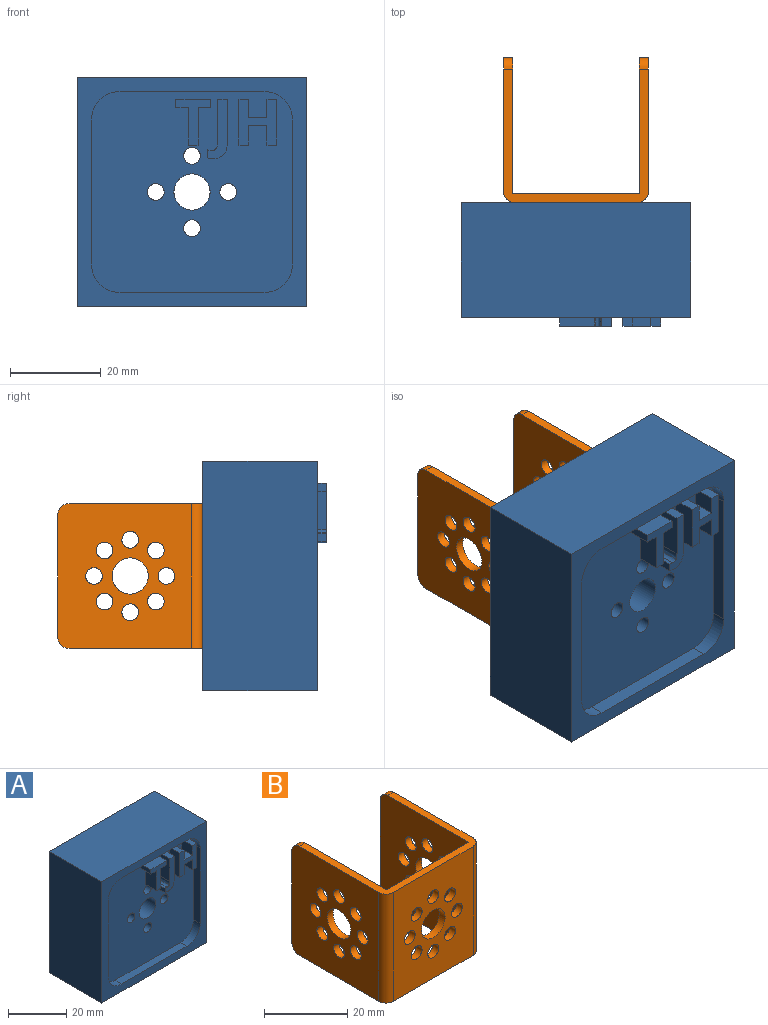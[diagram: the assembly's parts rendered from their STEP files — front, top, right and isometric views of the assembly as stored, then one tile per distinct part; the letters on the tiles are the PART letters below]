
ASSEMBLY  parts=2 mates=1
PART A: 53 faces, bbox 50.8x27.3x50.8 mm
  f0: plane 44.45x44.45mm, normal (0,-1,0), area 1734.2mm2, adj f7,f8,f9,f10,f11,f12,f13,f14
  f1: plane 50.8x50.8mm, normal (0,1,0), area 2487.4mm2, adj f2,f3,f4,f5,f15,f16,f17,f18
  f2: plane 50.8x25.4mm, normal (-1,0,0), area 1290.3mm2, adj f1,f3,f5,f6
  f3: plane 50.8x25.4mm, normal (0,0,-1), area 1290.3mm2, adj f1,f2,f4,f6
  f4: plane 50.8x25.4mm, normal (1,0,0), area 1290.3mm2, adj f1,f3,f5,f6
  f5: plane 50.8x25.4mm, normal (0,0,1), area 1290.3mm2, adj f1,f2,f4,f6
  f6: plane 50.8x50.8mm, normal (0,-1,0), area 639.5mm2, adj f2,f3,f4,f5,f7,f8,f9,f10
  f7: plane 31.75x3.18mm, normal (0,0,1), area 100.8mm2, adj f0,f6,f8,f14
  f8: cylinder r=6.35mm len=6.35mm, axis (0,-1,0), area 31.7mm2, adj f0,f6,f7,f9
  f9: plane 31.75x3.18mm, normal (-1,0,0), area 100.8mm2, adj f0,f6,f8,f10
  f10: cylinder r=6.35mm len=6.35mm, axis (0,-1,0), area 31.7mm2, adj f0,f6,f9,f11
  f11: plane 31.75x3.18mm, normal (0,0,-1), area 100.8mm2, adj f0,f6,f10,f12
  f12: cylinder r=6.35mm len=6.35mm, axis (0,-1,0), area 31.7mm2, adj f0,f6,f11,f13
  f13: plane 31.75x3.18mm, normal (1,0,0), area 100.8mm2, adj f0,f6,f12,f14
  f14: cylinder r=6.35mm len=6.35mm, axis (0,-1,0), area 31.7mm2, adj f0,f6,f7,f13
  f15: cylinder r=1.85mm len=22.23mm, axis (0,1,0), area 258.3mm2, adj f0,f1
  f16: cylinder r=4mm len=22.23mm, axis (0,1,0), area 558.6mm2, adj f0,f1
  f17: cylinder r=1.85mm len=22.23mm, axis (0,1,0), area 258.3mm2, adj f0,f1
  f18: cylinder r=1.85mm len=22.23mm, axis (0,1,0), area 258.3mm2, adj f0,f1
  f19: cylinder r=1.85mm len=22.23mm, axis (0,1,0), area 258.3mm2, adj f0,f1
  f20: plane 5.08x2.16mm, normal (0,0,-1), area 10.9mm2, adj f0,f21,f27,f28
  f21: plane 8.37x5.08mm, normal (1,0,0), area 42.5mm2, adj f0,f20,f22,f28
  f22: plane 5.08x2.76mm, normal (0,0,-1), area 14mm2, adj f0,f21,f23,f28
  f23: plane 5.08x1.79mm, normal (1,0,0), area 9.1mm2, adj f0,f22,f24,f28
  f24: plane 7.67x5.08mm, normal (0,0,1), area 39mm2, adj f0,f23,f25,f28
  f25: plane 5.08x1.79mm, normal (-1,0,0), area 9.1mm2, adj f0,f24,f26,f28
  f26: plane 5.08x2.76mm, normal (0,0,-1), area 14mm2, adj f0,f25,f27,f28
  f27: plane 8.37x5.08mm, normal (-1,0,0), area 42.5mm2, adj f0,f20,f26,f28
  f28: plane 10.16x7.67mm, normal (0,-1,0), area 31.8mm2, adj f20,f21,f22,f23,f24,f25,f26,f27
  f29: extruded ~5.08x1.27mm, area 6.5mm2, adj f0,f30,f38,f39
  f30: extruded ~5.08x2.41mm, area 13.5mm2, adj f0,f29,f31,f39
  f31: extruded ~5.08x2.71mm, area 14.7mm2, adj f0,f30,f32,f39
  f32: plane 9.51x5.08mm, normal (1,0,0), area 48.3mm2, adj f0,f31,f33,f39
  f33: plane 5.08x2.16mm, normal (0,0,1), area 10.9mm2, adj f0,f32,f34,f39
  f34: plane 9.52x5.08mm, normal (-1,0,0), area 48.4mm2, adj f0,f33,f35,f39
  f35: extruded ~5.08x1.38mm, area 7.3mm2, adj f0,f34,f36,f39
  f36: extruded ~5.08x1.02mm, area 5.9mm2, adj f0,f35,f37,f39
  f37: extruded ~5.08x1.01mm, area 5.2mm2, adj f0,f36,f38,f39
  f38: plane 5.08x1.79mm, normal (-1,0,0), area 9.1mm2, adj f0,f29,f37,f39
  f39: plane 13.15x4.49mm, normal (0,-1,0), area 30.9mm2, adj f29,f30,f31,f32,f33,f34,f35,f36
  f40: plane 5.08x2.15mm, normal (0,0,-1), area 10.9mm2, adj f0,f41,f51,f52
  f41: plane 10.16x5.08mm, normal (1,0,0), area 51.6mm2, adj f0,f40,f42,f52
  f42: plane 5.08x2.15mm, normal (0,0,1), area 10.9mm2, adj f0,f41,f43,f52
  f43: plane 5.08x3.98mm, normal (-1,0,0), area 20.2mm2, adj f0,f42,f44,f52
  f44: plane 5.08x4.02mm, normal (0,0,1), area 20.4mm2, adj f0,f43,f45,f52
  f45: plane 5.08x3.98mm, normal (1,0,0), area 20.2mm2, adj f0,f44,f46,f52
  f46: plane 5.08x2.16mm, normal (0,0,1), area 10.9mm2, adj f0,f45,f47,f52
  f47: plane 10.16x5.08mm, normal (-1,0,0), area 51.6mm2, adj f0,f46,f48,f52
  f48: plane 5.08x2.16mm, normal (0,0,-1), area 10.9mm2, adj f0,f47,f49,f52
  f49: plane 5.08x4.39mm, normal (1,0,0), area 22.3mm2, adj f0,f48,f50,f52
  f50: plane 5.08x4.02mm, normal (0,0,-1), area 20.4mm2, adj f0,f49,f51,f52
  f51: plane 5.08x4.39mm, normal (-1,0,0), area 22.3mm2, adj f0,f40,f50,f52
  f52: plane 10.16x8.33mm, normal (0,-1,0), area 51mm2, adj f40,f41,f42,f43,f44,f45,f46,f47
PART B: 43 faces, bbox 32x32x32 mm
  f0: plane 32x29.5mm, normal (-1,0,0), area 805mm2, adj f1,f3,f5,f10,f11,f12,f13,f14
  f1: plane 27x2mm, normal (0,1,0), area 54mm2, adj f0,f7,f38,f39
  f2: plane 27x2mm, normal (0,1,0), area 54mm2, adj f6,f9,f41,f42
  f3: plane 32x29.5mm, normal (0,0,-1), area 171.3mm2, adj f0,f4,f6,f7,f8,f9,f37,f39
  f4: plane 32x27mm, normal (0,-1,0), area 727.7mm2, adj f3,f5,f19,f20,f21,f22,f23,f24
  f5: plane 32x29.5mm, normal (0,0,1), area 171.3mm2, adj f0,f4,f6,f7,f8,f9,f37,f38
  f6: plane 32x29.5mm, normal (1,0,0), area 805mm2, adj f2,f3,f5,f28,f29,f30,f31,f32
  f7: plane 32x30mm, normal (1,0,0), area 821mm2, adj f1,f3,f5,f8,f10,f11,f12,f13
  f8: plane 32x28mm, normal (0,1,0), area 759.7mm2, adj f3,f5,f7,f9,f19,f20,f21,f22
  f9: plane 32x30mm, normal (-1,0,0), area 821mm2, adj f2,f3,f5,f8,f28,f29,f30,f31
  f10: cylinder r=4mm len=8mm, axis (-1,0,0), area 50.3mm2, adj f0,f7
  f11: cylinder r=1.85mm len=3.7mm, axis (-1,0,0), area 23.2mm2, adj f0,f7
  f12: cylinder r=1.85mm len=3.7mm, axis (-1,0,0), area 23.2mm2, adj f0,f7
  f13: cylinder r=1.85mm len=3.7mm, axis (-1,0,0), area 23.2mm2, adj f0,f7
  f14: cylinder r=1.85mm len=3.7mm, axis (-1,0,0), area 23.2mm2, adj f0,f7
  f15: cylinder r=1.85mm len=3.7mm, axis (-1,0,0), area 23.2mm2, adj f0,f7
  f16: cylinder r=1.85mm len=3.7mm, axis (-1,0,0), area 23.2mm2, adj f0,f7
  f17: cylinder r=1.85mm len=3.7mm, axis (-1,0,0), area 23.2mm2, adj f0,f7
  f18: cylinder r=1.85mm len=3.7mm, axis (-1,0,0), area 23.2mm2, adj f0,f7
  f19: cylinder r=1.85mm len=3.7mm, axis (0,1,0), area 23.2mm2, adj f4,f8
  f20: cylinder r=1.85mm len=3.7mm, axis (0,1,0), area 23.2mm2, adj f4,f8
  f21: cylinder r=1.85mm len=3.7mm, axis (0,1,0), area 23.2mm2, adj f4,f8
  f22: cylinder r=1.85mm len=3.7mm, axis (0,1,0), area 23.2mm2, adj f4,f8
  f23: cylinder r=1.85mm len=3.7mm, axis (0,1,0), area 23.2mm2, adj f4,f8
  f24: cylinder r=1.85mm len=3.7mm, axis (0,1,0), area 23.2mm2, adj f4,f8
  f25: cylinder r=1.85mm len=3.7mm, axis (0,1,0), area 23.2mm2, adj f4,f8
  f26: cylinder r=1.85mm len=3.7mm, axis (0,1,0), area 23.2mm2, adj f4,f8
  f27: cylinder r=4mm len=8mm, axis (0,-1,0), area 50.3mm2, adj f4,f8
  f28: cylinder r=4mm len=8mm, axis (1,0,0), area 50.3mm2, adj f6,f9
  f29: cylinder r=1.85mm len=3.7mm, axis (1,0,0), area 23.2mm2, adj f6,f9
  f30: cylinder r=1.85mm len=3.7mm, axis (1,0,0), area 23.2mm2, adj f6,f9
  f31: cylinder r=1.85mm len=3.7mm, axis (1,0,0), area 23.2mm2, adj f6,f9
  f32: cylinder r=1.85mm len=3.7mm, axis (1,0,0), area 23.2mm2, adj f6,f9
  f33: cylinder r=1.85mm len=3.7mm, axis (1,0,0), area 23.2mm2, adj f6,f9
  f34: cylinder r=1.85mm len=3.7mm, axis (1,0,0), area 23.2mm2, adj f6,f9
  f35: cylinder r=1.85mm len=3.7mm, axis (1,0,0), area 23.2mm2, adj f6,f9
  f36: cylinder r=1.85mm len=3.7mm, axis (1,0,0), area 23.2mm2, adj f6,f9
  f37: cylinder r=2.5mm len=32mm, axis (0,0,1), area 125.7mm2, adj f0,f3,f4,f5
  f38: cylinder r=2.5mm len=2.5mm, axis (1,0,0), area 7.9mm2, adj f0,f1,f5,f7
  f39: cylinder r=2.5mm len=2.5mm, axis (1,0,0), area 7.9mm2, adj f0,f1,f3,f7
  f40: cylinder r=2.5mm len=32mm, axis (0,0,-1), area 125.7mm2, adj f3,f4,f5,f6
  f41: cylinder r=2.5mm len=2.5mm, axis (1,0,0), area 7.9mm2, adj f2,f5,f6,f9
  f42: cylinder r=2.5mm len=2.5mm, axis (1,0,0), area 7.9mm2, adj f2,f3,f6,f9
PLACE A t=(-57.96,-96.21,-14.95)mm
PLACE B t=(-32.56,-96.21,10.45)mm
MATE fastened A.f16 <-> B.f27  axis (0,1,0) through (-32.56,-96.21,10.45)mm
